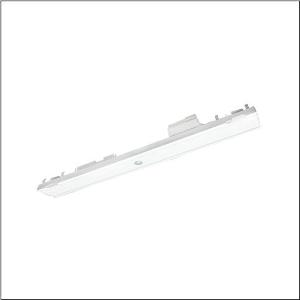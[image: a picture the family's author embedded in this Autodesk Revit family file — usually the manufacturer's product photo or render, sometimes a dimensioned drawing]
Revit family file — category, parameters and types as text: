
# Revit family: licross_r_56tl1e7c4x31_1f0a
name_source: partatom
category: Lighting Fixtures
units: mm (PartAtom-declared; Revit-internal decimal feet)

## family parameters
Cut with Voids When Loaded = No
Host = Face
Light Source = No
Part Type = Normal
Room Calculation Point = No
Round Connector Dimension = Use Diameter
Shared = No

## types (1)
- Licross® (1 x LED, 320 lm, 3.9 W, 4000K)
    Apparent Load = 4 VA
    CIE Flux Codes = 63 91 97 100 100
    Color Rendering = 70
    Color Temperature = 4000K
    Default Elevation = 1800 mm
    Description = Licross®, luminaire insert, of sheet steel, coil coated, white, length: 500mm, width: 59mm, height: 60mm, mounting height: 7..17m, emergency light element,LED rated luminous flux: 320lm, light colour: 740, control gear: CEAG, with plug, 6-pole, with phase selection, mains connection: 220..240V, AC/DC, 0/50..60Hz, rated input power: 3.9W, halogen-free wiring, for trunking rail, 9..14-core, for emergency light function, supply monitoring module CEAG, with address switch, choice between two emergency light lines via tool-free moving of contact pin prior to installation in trunking rail, primary light control with lens, of PMMA, primary optical cover: cover, of PMMA, light emission: direct distribution, primary light characteristic: asymmetric,  for escape and rescue routes, compatible with all CEAG STAR technology systems (ZB-S, DG-S (DualGuard-S), LP-STAR, AT-S+), protection rating (complete): IP40, insulation class (complete): insulation class I (protective earthing), certification: CE, UKCA, protection symbol: D if used in an environment without relevant dust loads, impact resistance: IK06, permissible ambient temperature for indoor applications: -20..+40°C, packaging unit: 1 piece
    Height = 60 mm  [stored 0.19685 ft]
    Lamp = 1 x LED
    Lamp Light Flux = 320 lm
    Lamp Power = 3.9 W
    Lamp count = 1
    Length = 500 mm
    Luminous efficacy = 82 lm/W
    Manufacturer = Siteco
    ModVariant = No
    Model = 56TL1E7C4X31
    Mounting Place = Ceiling
    Mounting Type = Pendant
    Number of Poles = 1
    OnlyDefault = Yes
    Power Factor = 1
    Product Name = Licross®
    Product group = luminaire insert
    ProductGroupID = 901
    Protection Class = Protection class I
    Protection Degree = IP 40
    RLX_Detail_Level = 1
    RLX_Emergency_Light_Flux = 0 lm
    RLX_Emergency_Type = 0
    RLX_Emergency_Type_DB = No
    RlxData = <blob elided: 31265 chars, md5=81dac3cf>
    Socket = socket
    Standby Power = 0 W
    System Light Flux = 320 lm
    System Power = 4 W
    Type Comments = Product without accessories
    Type Image = l_1251804.jpg
    URL = http://relux.com
    VarID = ---
    Voltage = 0 V
    Weight = 0.00 kg
    Width = 59 mm

note: [stored X ft] marks values corroborated as IEEE doubles in the binary element streams (Revit-internal decimal feet)

## geometry (parser evidence)
native form markers: Blend x4, Sweep x10
no freeform markers — native parametric forms only
